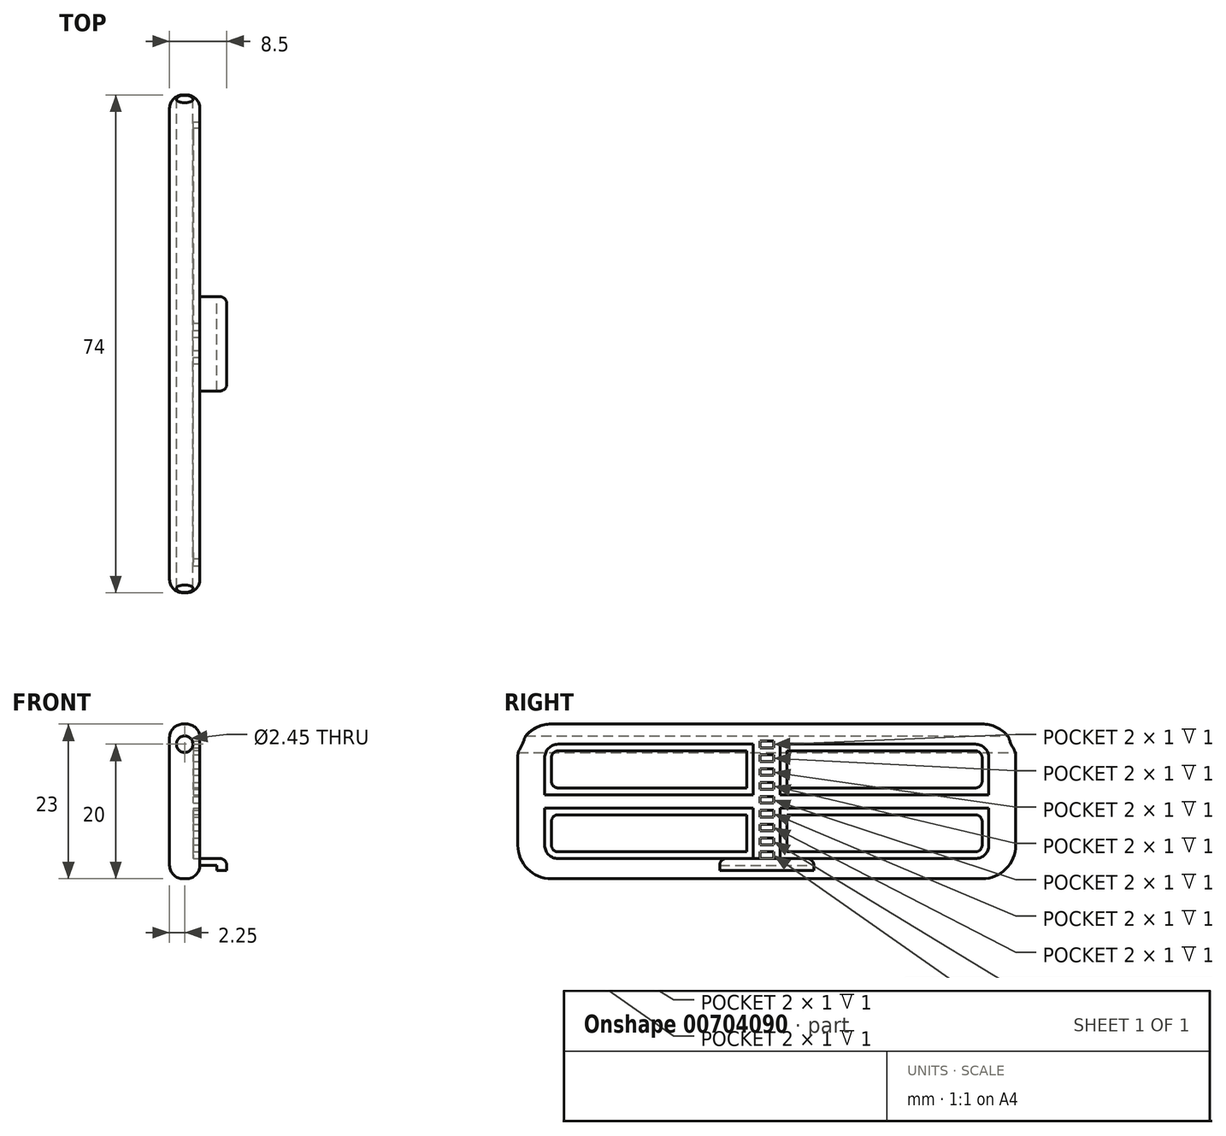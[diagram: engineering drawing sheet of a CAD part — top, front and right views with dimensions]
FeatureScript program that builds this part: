
annotation { "Feature Type Name" : "Feature", "Feature Type Description" : "" }
export const myFeature = defineFeature(function(context is Context, id is Id, definition is map)
    precondition{}
    {
        {
            var Q0;
            Q0=qCreatedBy(makeId("Right.planeOp"),FACE);
            var sketch = newSketch(context, id + "F0", { "sketchPlane" : qUnion([Q0])});
            skLineSegment(sketch, "E0.bottom", {"start": v(5, 0) * mm, "end": v(69, 0) * mm});
            skLineSegment(sketch, "E0.top", {"start": v(5, 23) * mm, "end": v(69, 23) * mm});
            skLineSegment(sketch, "E0.left", {"start": v(0, 5) * mm, "end": v(0, 18) * mm});
            skLineSegment(sketch, "E0.right", {"start": v(74, 5) * mm, "end": v(74, 18) * mm});
            skPoint(sketch, "E1.visualSharp", {"position": v(0, 23) * mm});
            skArc(sketch, "E1.filletArc", {"start": v(5, 23) * mm, "mid": v(1.46, 21.54) * mm, "end": v(0, 18) * mm});
            skPoint(sketch, "E2.visualSharp", {"position": v(74, 23) * mm});
            skArc(sketch, "E2.filletArc", {"start": v(74, 18) * mm, "mid": v(72.54, 21.54) * mm, "end": v(69, 23) * mm});
            skPoint(sketch, "E3.visualSharp", {"position": v(74, 0) * mm});
            skArc(sketch, "E3.filletArc", {"start": v(69, 0) * mm, "mid": v(72.54, 1.46) * mm, "end": v(74, 5) * mm});
            skPoint(sketch, "E4.visualSharp", {"position": v(0, 0) * mm});
            skArc(sketch, "E4.filletArc", {"start": v(0, 5) * mm, "mid": v(1.46, 1.46) * mm, "end": v(5, 0) * mm});
            skSolve(sketch);
        }
        {
            var Q0;
            Q0=qSketchRegion(id+"F0",true);
            extrude(context, id + "F1", {"entities" : qUnion([Q0]), "depth" : 4.5 * mm});
        }
        {
            var Q0;
            Q0=makeQuery(id+"F1.opExtrude","SWEPT_FACE",FACE,{"disambiguationData":[OSD([sQuery(id+"F0.wireOp",EDGE,"E0.right")])]});
            var sketch = newSketch(context, id + "F2", { "sketchPlane" : qUnion([Q0])});
            skCircle(sketch, "E5", {"center": v(-2.25, 20) * mm, "radius": 1.23 * mm});
            skSolve(sketch);
        }
        {
            var Q0;
            Q0=qSketchRegion(id+"F2",true);
            var Q1;
            Q1=makeQuery(id+"F1.opExtrude","SWEPT_FACE",FACE,{"disambiguationData":[OSD([sQuery(id+"F0.wireOp",EDGE,"E0.left")])]});
            extrude(context, id + "F3", {"entities" : qUnion([Q0]), "operationType" : NewBodyOperationType.REMOVE, "endBound" : BoundingType.UP_TO_SURFACE, "oppositeDirection" : true, "endBoundEntityFace" : qUnion([Q1]), "depth" : 25 * mm});
        }
        {
            var Q0;
            Q0=makeQuery(id+"F1.opExtrude","CAP_EDGE",EDGE,{"disambiguationData":[OSD([sQuery(id+"F0.wireOp",EDGE,"E0.top")])],"isStart":true});
            var Q1;
            Q1=makeQuery(id+"F1.opExtrude","CAP_EDGE",EDGE,{"disambiguationData":[OSD([sQuery(id+"F0.wireOp",EDGE,"E0.top")])],"isStart":false});
            fillet(context, id + "F4", {"entities" : qUnion([Q0, Q1]), "radius" : 2 * mm, "tangentPropagation" : true, "allowEdgeOverflow" : false});
        }
        {
            var Q0;
            Q0=makeQuery(id+"F1.opExtrude","CAP_FACE",FACE,{"disambiguationData":[OSD([sQuery(id+"F0.wireOp",EDGE,"E0.bottom"),sQuery(id+"F0.wireOp",EDGE,"E0.top"),sQuery(id+"F0.wireOp",EDGE,"E0.left"),sQuery(id+"F0.wireOp",EDGE,"E0.right")])],"isStart":false});
            var sketch = newSketch(context, id + "F5", { "sketchPlane" : qUnion([Q0])});
            skLineSegment(sketch, "E6.bottom", {"start": v(6, 20) * mm, "end": v(35, 20) * mm});
            skLineSegment(sketch, "E6.top", {"start": v(6, 3) * mm, "end": v(35, 3) * mm});
            skLineSegment(sketch, "E6.left", {"start": v(4, 18) * mm, "end": v(4, 12.5) * mm});
            skLineSegment(sketch, "E6.right", {"start": v(35, 20) * mm, "end": v(35, 12.5) * mm});
            skLineSegment(sketch, "E7.bottom", {"start": v(39, 20) * mm, "end": v(68, 20) * mm});
            skLineSegment(sketch, "E7.top", {"start": v(39, 3) * mm, "end": v(68, 3) * mm});
            skLineSegment(sketch, "E7.left", {"start": v(39, 20) * mm, "end": v(39, 12.5) * mm});
            skLineSegment(sketch, "E7.right", {"start": v(70, 18) * mm, "end": v(70, 12.5) * mm});
            skLineSegment(sketch, "E8", {"start": v(4, 12.5) * mm, "end": v(35, 12.5) * mm});
            skLineSegment(sketch, "E9", {"start": v(4, 10.5) * mm, "end": v(35, 10.5) * mm});
            skLineSegment(sketch, "E10.trimOffspring", {"start": v(39, 12.5) * mm, "end": v(70, 12.5) * mm});
            skLineSegment(sketch, "E11.trimOffspring", {"start": v(35, 10.5) * mm, "end": v(35, 3) * mm});
            skLineSegment(sketch, "E12.trimOffspring", {"start": v(39, 10.5) * mm, "end": v(70, 10.5) * mm});
            skLineSegment(sketch, "E13.trimOffspring", {"start": v(39, 10.5) * mm, "end": v(39, 3) * mm});
            skLineSegment(sketch, "E14.trimOffspring", {"start": v(70, 10.5) * mm, "end": v(70, 5) * mm});
            skLineSegment(sketch, "E15.trimOffspring", {"start": v(4, 10.5) * mm, "end": v(4, 5) * mm});
            skLineSegment(sketch, "E16", {"start": v(37, 21) * mm, "end": v(37, 2) * mm, "construction": true});
            skLineSegment(sketch, "E17", {"start": v(2, 11.5) * mm, "end": v(72, 11.5) * mm, "construction": true});
            skPoint(sketch, "E18.visualSharp", {"position": v(4, 20) * mm});
            skArc(sketch, "E18.filletArc", {"start": v(6, 20) * mm, "mid": v(4.59, 19.41) * mm, "end": v(4, 18) * mm});
            skPoint(sketch, "E19.visualSharp", {"position": v(70, 20) * mm});
            skArc(sketch, "E19.filletArc", {"start": v(70, 18) * mm, "mid": v(69.41, 19.41) * mm, "end": v(68, 20) * mm});
            skPoint(sketch, "E20.visualSharp", {"position": v(70, 3) * mm});
            skArc(sketch, "E20.filletArc", {"start": v(68, 3) * mm, "mid": v(69.41, 3.59) * mm, "end": v(70, 5) * mm});
            skPoint(sketch, "E21.visualSharp", {"position": v(4, 3) * mm});
            skArc(sketch, "E21.filletArc", {"start": v(4, 5) * mm, "mid": v(4.59, 3.59) * mm, "end": v(6, 3) * mm});
            skSolve(sketch);
        }
        {
            var Q0;
            Q0=qSketchRegion(id+"F5",true);
            extrude(context, id + "F6", {"entities" : qUnion([Q0]), "operationType" : NewBodyOperationType.REMOVE, "oppositeDirection" : true, "depth" : 1 * mm});
        }
        {
            var Q0;
            Q0=makeQuery(id+"F1.opExtrude","CAP_FACE",FACE,{"disambiguationData":[OSD([sQuery(id+"F0.wireOp",EDGE,"E0.bottom"),sQuery(id+"F0.wireOp",EDGE,"E0.top"),sQuery(id+"F0.wireOp",EDGE,"E0.left"),sQuery(id+"F0.wireOp",EDGE,"E0.right")])],"isStart":false});
            var sketch = newSketch(context, id + "F7", { "sketchPlane" : qUnion([Q0])});
            skLineSegment(sketch, "E22.bottom", {"start": v(36, 3) * mm, "end": v(38, 3) * mm});
            skLineSegment(sketch, "E22.top", {"start": v(36, 4) * mm, "end": v(38, 4) * mm});
            skLineSegment(sketch, "E22.left", {"start": v(36, 3) * mm, "end": v(36, 4) * mm});
            skLineSegment(sketch, "E22.right", {"start": v(38, 3) * mm, "end": v(38, 4) * mm});
            skLineSegment(sketch, "E23.1.0.0", {"start": v(36, 5.06) * mm, "end": v(38, 5.06) * mm});
            skLineSegment(sketch, "E23.1.0.1", {"start": v(36, 6.06) * mm, "end": v(38, 6.06) * mm});
            skLineSegment(sketch, "E23.1.0.2", {"start": v(36, 5.06) * mm, "end": v(36, 6.06) * mm});
            skLineSegment(sketch, "E23.1.0.3", {"start": v(38, 5.06) * mm, "end": v(38, 6.06) * mm});
            skLineSegment(sketch, "E23.2.0.0", {"start": v(36, 7.12) * mm, "end": v(38, 7.12) * mm});
            skLineSegment(sketch, "E23.2.0.1", {"start": v(36, 8.12) * mm, "end": v(38, 8.12) * mm});
            skLineSegment(sketch, "E23.2.0.2", {"start": v(36, 7.12) * mm, "end": v(36, 8.12) * mm});
            skLineSegment(sketch, "E23.2.0.3", {"start": v(38, 7.12) * mm, "end": v(38, 8.12) * mm});
            skLineSegment(sketch, "E23.direction1", {"start": v(36, 3) * mm, "end": v(36, 5.06) * mm, "construction": true});
            skLineSegment(sketch, "E24.0.3.0", {"start": v(36, 9.18) * mm, "end": v(38, 9.18) * mm});
            skLineSegment(sketch, "E24.3.3.0", {"start": v(36, 10.18) * mm, "end": v(38, 10.18) * mm});
            skLineSegment(sketch, "E24.6.3.0", {"start": v(36, 9.18) * mm, "end": v(36, 10.18) * mm});
            skLineSegment(sketch, "E24.9.3.0", {"start": v(38, 9.18) * mm, "end": v(38, 10.18) * mm});
            skLineSegment(sketch, "E24.0.4.0", {"start": v(36, 11.24) * mm, "end": v(38, 11.24) * mm});
            skLineSegment(sketch, "E24.3.4.0", {"start": v(36, 12.24) * mm, "end": v(38, 12.24) * mm});
            skLineSegment(sketch, "E24.6.4.0", {"start": v(36, 11.24) * mm, "end": v(36, 12.24) * mm});
            skLineSegment(sketch, "E24.9.4.0", {"start": v(38, 11.24) * mm, "end": v(38, 12.24) * mm});
            skLineSegment(sketch, "E25.0.5.0", {"start": v(36, 13.3) * mm, "end": v(38, 13.3) * mm});
            skLineSegment(sketch, "E25.3.5.0", {"start": v(36, 14.3) * mm, "end": v(38, 14.3) * mm});
            skLineSegment(sketch, "E25.6.5.0", {"start": v(36, 13.3) * mm, "end": v(36, 14.3) * mm});
            skLineSegment(sketch, "E25.9.5.0", {"start": v(38, 13.3) * mm, "end": v(38, 14.3) * mm});
            skLineSegment(sketch, "E25.0.6.0", {"start": v(36, 15.36) * mm, "end": v(38, 15.36) * mm});
            skLineSegment(sketch, "E25.3.6.0", {"start": v(36, 16.36) * mm, "end": v(38, 16.36) * mm});
            skLineSegment(sketch, "E25.6.6.0", {"start": v(36, 15.36) * mm, "end": v(36, 16.36) * mm});
            skLineSegment(sketch, "E25.9.6.0", {"start": v(38, 15.36) * mm, "end": v(38, 16.36) * mm});
            skLineSegment(sketch, "E25.0.7.0", {"start": v(36, 17.42) * mm, "end": v(38, 17.42) * mm});
            skLineSegment(sketch, "E25.3.7.0", {"start": v(36, 18.42) * mm, "end": v(38, 18.42) * mm});
            skLineSegment(sketch, "E25.6.7.0", {"start": v(36, 17.42) * mm, "end": v(36, 18.42) * mm});
            skLineSegment(sketch, "E25.9.7.0", {"start": v(38, 17.42) * mm, "end": v(38, 18.42) * mm});
            skLineSegment(sketch, "E26.0.8.0", {"start": v(36, 19.48) * mm, "end": v(38, 19.48) * mm});
            skLineSegment(sketch, "E26.3.8.0", {"start": v(36, 20.48) * mm, "end": v(38, 20.48) * mm});
            skLineSegment(sketch, "E26.6.8.0", {"start": v(36, 19.48) * mm, "end": v(36, 20.48) * mm});
            skLineSegment(sketch, "E26.9.8.0", {"start": v(38, 19.48) * mm, "end": v(38, 20.48) * mm});
            skSolve(sketch);
        }
        {
            var Q0;
            Q0=qSketchRegion(id+"F7",true);
            extrude(context, id + "F8", {"entities" : qUnion([Q0]), "operationType" : NewBodyOperationType.REMOVE, "oppositeDirection" : true, "depth" : 1 * mm});
        }
        {
            var Q0;
            Q0=makeQuery(id+"F6.boolean.opBoolean","COPY",FACE,{"derivedFrom":makeQuery(id+"F6.opExtrude","CAP_FACE",FACE,{"disambiguationData":[OSD([sQuery(id+"F5.wireOp",EDGE,"E7.top"),sQuery(id+"F5.wireOp",EDGE,"E12.trimOffspring"),sQuery(id+"F5.wireOp",EDGE,"E13.trimOffspring"),sQuery(id+"F5.wireOp",EDGE,"E14.trimOffspring")])],"isStart":false})});
            var sketch = newSketch(context, id + "F9", { "sketchPlane" : qUnion([Q0])});
            skLineSegment(sketch, "E27.top", {"start": v(6, 4) * mm, "end": v(34, 4) * mm});
            skLineSegment(sketch, "E28", {"start": v(37, 2) * mm, "end": v(37, 21) * mm, "construction": true});
            skLineSegment(sketch, "E29.bottom", {"start": v(6, 9.5) * mm, "end": v(34, 9.5) * mm});
            skLineSegment(sketch, "E29.left", {"start": v(5, 8.5) * mm, "end": v(5, 5) * mm});
            skLineSegment(sketch, "E29.right", {"start": v(34, 9.5) * mm, "end": v(34, 4) * mm});
            skLineSegment(sketch, "E30.bottom", {"start": v(6, 19) * mm, "end": v(34, 19) * mm});
            skLineSegment(sketch, "E30.left", {"start": v(5, 18) * mm, "end": v(5, 14.5) * mm});
            skPoint(sketch, "E31.visualSharp", {"position": v(5, 19) * mm});
            skArc(sketch, "E31.filletArc", {"start": v(6, 19) * mm, "mid": v(5.3, 18.7) * mm, "end": v(5, 18) * mm});
            skLineSegment(sketch, "E32", {"start": v(34, 19) * mm, "end": v(34, 13.5) * mm});
            skLineSegment(sketch, "E33", {"start": v(34, 13.5) * mm, "end": v(6, 13.5) * mm});
            skPoint(sketch, "E34.orphan", {"position": v(34, 0) * mm});
            skPoint(sketch, "E35.visualSharp", {"position": v(5, 13.5) * mm});
            skArc(sketch, "E35.filletArc", {"start": v(5, 14.5) * mm, "mid": v(5.3, 13.8) * mm, "end": v(6, 13.5) * mm});
            skPoint(sketch, "E36.visualSharp", {"position": v(5, 9.5) * mm});
            skArc(sketch, "E36.filletArc", {"start": v(6, 9.5) * mm, "mid": v(5.3, 9.2) * mm, "end": v(5, 8.5) * mm});
            skPoint(sketch, "E37.visualSharp", {"position": v(5, 4) * mm});
            skArc(sketch, "E37.filletArc", {"start": v(5, 5) * mm, "mid": v(5.3, 4.3) * mm, "end": v(6, 4) * mm});
            skArc(sketch, "E38.MirrorCS", {"start": v(68, 9.5) * mm, "mid": v(68.7, 9.2) * mm, "end": v(69, 8.5) * mm});
            skArc(sketch, "E39.MirrorCS", {"start": v(69, 14.5) * mm, "mid": v(68.7, 13.8) * mm, "end": v(68, 13.5) * mm});
            skArc(sketch, "E40.MirrorCS", {"start": v(68, 19) * mm, "mid": v(68.7, 18.7) * mm, "end": v(69, 18) * mm});
            skArc(sketch, "E41.MirrorCS", {"start": v(69, 5) * mm, "mid": v(68.7, 4.3) * mm, "end": v(68, 4) * mm});
            skLineSegment(sketch, "E42.MirrorCS", {"start": v(40, 9.5) * mm, "end": v(40, 4) * mm});
            skPoint(sketch, "E43.MirrorP", {"position": v(69, 9.5) * mm});
            skLineSegment(sketch, "E44.MirrorCS", {"start": v(40, 19) * mm, "end": v(40, 13.5) * mm});
            skLineSegment(sketch, "E45.MirrorCS", {"start": v(68, 4) * mm, "end": v(40, 4) * mm});
            skLineSegment(sketch, "E46.MirrorCS", {"start": v(68, 9.5) * mm, "end": v(40, 9.5) * mm});
            skPoint(sketch, "E47.MirrorP", {"position": v(69, 13.5) * mm});
            skPoint(sketch, "E48.MirrorP", {"position": v(69, 19) * mm});
            skLineSegment(sketch, "E49.MirrorCS", {"start": v(69, 8.5) * mm, "end": v(69, 5) * mm});
            skLineSegment(sketch, "E50.MirrorCS", {"start": v(68, 19) * mm, "end": v(40, 19) * mm});
            skLineSegment(sketch, "E51.MirrorCS", {"start": v(40, 13.5) * mm, "end": v(68, 13.5) * mm});
            skPoint(sketch, "E52.MirrorP", {"position": v(69, 4) * mm});
            skLineSegment(sketch, "E53.MirrorCS", {"start": v(69, 18) * mm, "end": v(69, 14.5) * mm});
            skPoint(sketch, "E54.MirrorP", {"position": v(40, 0) * mm});
            skSolve(sketch);
        }
        {
            var Q0;
            Q0=qSketchRegion(id+"F9",true);
            extrude(context, id + "F10", {"entities" : qUnion([Q0]), "operationType" : NewBodyOperationType.ADD, "depth" : 1 * mm, "offsetDistance" : 25 * mm});
        }
        {
            var Q0;
            Q0=makeQuery(id+"F1.opExtrude","CAP_FACE",FACE,{"disambiguationData":[OSD([sQuery(id+"F0.wireOp",EDGE,"E0.bottom"),sQuery(id+"F0.wireOp",EDGE,"E0.top"),sQuery(id+"F0.wireOp",EDGE,"E0.left"),sQuery(id+"F0.wireOp",EDGE,"E0.right"),sQuery(id+"F0.wireOp",EDGE,"E1.filletArc"),sQuery(id+"F0.wireOp",EDGE,"E2.filletArc"),sQuery(id+"F0.wireOp",EDGE,"E3.filletArc"),sQuery(id+"F0.wireOp",EDGE,"E4.filletArc")])],"isStart":false});
            var sketch = newSketch(context, id + "F11", { "sketchPlane" : qUnion([Q0])});
            skLineSegment(sketch, "E55.bottom", {"start": v(30, 3) * mm, "end": v(44, 3) * mm});
            skLineSegment(sketch, "E55.top", {"start": v(30, 2) * mm, "end": v(44, 2) * mm});
            skLineSegment(sketch, "E55.left", {"start": v(30, 3) * mm, "end": v(30, 2) * mm});
            skLineSegment(sketch, "E55.right", {"start": v(44, 3) * mm, "end": v(44, 2) * mm});
            skSolve(sketch);
        }
        {
            var Q0;
            Q0=qSketchRegion(id+"F11",true);
            extrude(context, id + "F12", {"entities" : qUnion([Q0]), "operationType" : NewBodyOperationType.ADD, "depth" : 4 * mm, "offsetDistance" : 25 * mm});
        }
        {
            var Q0;
            Q0=makeQuery(id+"F12.opExtrude","SWEPT_FACE",FACE,{"disambiguationData":[OSD([sQuery(id+"F11.wireOp",EDGE,"E55.top")])]});
            var sketch = newSketch(context, id + "F13", { "sketchPlane" : qUnion([Q0])});
            skLineSegment(sketch, "E56.bottom", {"start": v(8.5, -30) * mm, "end": v(7, -30) * mm});
            skLineSegment(sketch, "E56.top", {"start": v(8.5, -44) * mm, "end": v(7, -44) * mm});
            skLineSegment(sketch, "E56.left", {"start": v(8.5, -30) * mm, "end": v(8.5, -44) * mm});
            skLineSegment(sketch, "E56.right", {"start": v(7, -30) * mm, "end": v(7, -44) * mm});
            skSolve(sketch);
        }
        {
            var Q0;
            Q0=qSketchRegion(id+"F13",true);
            extrude(context, id + "F14", {"entities" : qUnion([Q0]), "operationType" : NewBodyOperationType.ADD, "depth" : .75 * mm, "offsetDistance" : 25 * mm});
        }
        {
            var Q0;
            Q0=makeQuery(id+"F12.opExtrude","CAP_EDGE",EDGE,{"disambiguationData":[OSD([sQuery(id+"F11.wireOp",EDGE,"E55.bottom")])],"isStart":false});
            var Q1;
            Q1=makeQuery(id+"F12.opExtrude","SWEPT_EDGE",EDGE,{"disambiguationData":[OSD([sQuery(id+"F5.wireOp",EDGE,"E6.top"),sQuery(id+"F11.wireOp",EDGE,"E55.bottom"),sQuery(id+"F11.wireOp",EDGE,"E55.left")])]});
            var Q2;
            Q2=makeQuery(id+"F12.opExtrude","SWEPT_EDGE",EDGE,{"disambiguationData":[OSD([sQuery(id+"F5.wireOp",EDGE,"E7.top"),sQuery(id+"F11.wireOp",EDGE,"E55.bottom"),sQuery(id+"F11.wireOp",EDGE,"E55.right")])]});
            var Q3;
            Q3=makeQuery(id+"F14.boolean.opBoolean","MERGE",EDGE,{"derivedFrom":[makeQuery(id+"F12.opExtrude","CAP_EDGE",EDGE,{"disambiguationData":[OSD([sQuery(id+"F11.wireOp",EDGE,"E55.right")])],"isStart":false}),makeQuery(id+"F14.opExtrude","SWEPT_EDGE",EDGE,{"disambiguationData":[OSD([sQuery(id+"F13.wireOp",EDGE,"E56.top"),sQuery(id+"F13.wireOp",EDGE,"E56.left")])]})]});
            var Q4;
            Q4=makeQuery(id+"F14.boolean.opBoolean","MERGE",EDGE,{"derivedFrom":[makeQuery(id+"F12.opExtrude","CAP_EDGE",EDGE,{"disambiguationData":[OSD([sQuery(id+"F11.wireOp",EDGE,"E55.left")])],"isStart":false}),makeQuery(id+"F14.opExtrude","SWEPT_EDGE",EDGE,{"disambiguationData":[OSD([sQuery(id+"F13.wireOp",EDGE,"E56.bottom"),sQuery(id+"F13.wireOp",EDGE,"E56.left")])]})]});
            fillet(context, id + "F15", {"entities" : qUnion([Q0, Q1, Q2, Q3, Q4]), "radius" : 1 * mm, "tangentPropagation" : true, "allowEdgeOverflow" : false});
        }
    });
